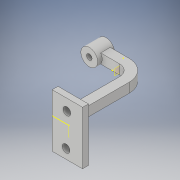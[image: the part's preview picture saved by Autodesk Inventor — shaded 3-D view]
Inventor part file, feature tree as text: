
AUTODESK INVENTOR PART (.ipt)
format: ipt  version: 2019 (Build 230136000, 136)  size: 235,008 bytes
history: native  units: in
note: dims shown in document units (in); Inventor stores cm internally (conversion verified against a paired STEP export)
features: sketch x35, extrude x6, hole x5, thicken_offset x4, plane x2, sweep x1
ambient origin geometry x8: Origin, YZ Plane, XZ Plane, XY Plane, X Axis, Y Axis, Z Axis, Center Point
bodies: Solid1 (feature_tree)
feature tree (53):
  sketch  "Sketch1"  dims[d1=0.5in d2=0.0in]
  extrude  "Extrusion1"  Depth=1.0in
  hole  "Hole1"  [1 undecoded]
  plane  "Work Plane1"
  sweep  "Sweep1"
  sketch  "Sketch8"  dims[d30=0.43in d32=0.43in d33=0.0in]
  sketch  "Sketch9"  dims[d36=0.26in d37=0.43in d38=0.0in]
  sketch  "Sketch10"  dims[d39=1.0in d40=0.0in d41=0.3in]
  sketch  "Sketch11"  dims[d42=0.3in d43=0.3in]
  sketch  "Sketch12"  dims[d44=0.3in d45=0.0in]
  sketch  "Sketch13"  dims[d46=0.6in d47=0.0in d48=0.12in]
  extrude  "Extrusion4"  TaperAngle=0.0deg  [1 undecoded]
  extrude  "Extrusion5"  Depth=0.43in TaperAngle=0.0deg
  sketch  "Sketch15"  dims[d51=0.04in d52=0.25in d53=0.0in]
  sketch  "Sketch16"  dims[d54=0.346in d55=0.75in d56=0.375in d57=0.25in d58=0.5635in d59=1.0in d60=0.8108in]
  sketch  "Sketch17"  dims[d61=0.346in d62=0.75in d63=0.375in d64=0.25in d65=0.5635in d66=1.0in d67=0.8108in]
  sketch  "Sketch18"  dims[d68=1.0in d69=1.375in d70=0.0in d71=0.0in]
  sketch  "Sketch19"  dims[d72=0.345in d73=0.75in d74=0.375in d75=0.25in d76=0.5635in d77=1.0in d78=0.8108in]
  sketch  "Sketch20"  dims[d79=0.345in d80=0.75in d81=0.375in d82=0.25in d83=0.5635in d84=1.0in d85=0.8108in]
  sketch  "Sketch21"
  sketch  "Sketch22"
  sketch  "Sketch23"
  extrude  "Extrusion6"  Depth=0.43in TaperAngle=0.0deg
  sketch  "Sketch25"
  sketch  "Sketch26"
  sketch  "Sketch27"
  sketch  "Sketch28"
  sketch  "Sketch29"
  sketch  "Sketch30"
  thicken_offset  "Thicken1"
  thicken_offset  "Thicken2"
  sketch  "Sketch31"
  plane  "Work Plane2"
  extrude  "Extrusion7"  Depth=1.0in
  thicken_offset  "Thicken3"
  thicken_offset  "Thicken4"
  hole  "Hole2"  [1 undecoded]
  hole  "Hole3"  [1 undecoded]
  sketch  "Sketch36"
  extrude  "Extrusion8"  Depth=0.12in
  hole  "Hole4"  [1 undecoded]
  hole  "Hole5"  [1 undecoded]
  sketch  "Sketch2"  dims[d3=0.247in d4=0.75in d5=0.375in d6=0.25in d7=0.5635in d8=1.0in d9=0.8108in d10=0.125in]
  sketch  "Sketch3"  dims[d11=0.125in d12=0.2in]
  sketch  "Sketch4"  dims[d13=0.5in d14=0.2in]
  sketch  "Sketch5"  dims[d15=0.0in d16=0.0in d17=0.0in]
  sketch  "Sketch14"  dims[d49=0.12in d50=0.04in]
  sketch  "Sketch24"
  sketch  "Sketch32"
  sketch  "Sketch33"
  sketch  "Sketch34"
  sketch  "Sketch37"
  sketch  "Sketch38"
note: 6 required parameter values undecoded (feature->parameter linkage not recoverable at this tier; creation-order binding heuristic only, values carry confidence <= 0.55)
